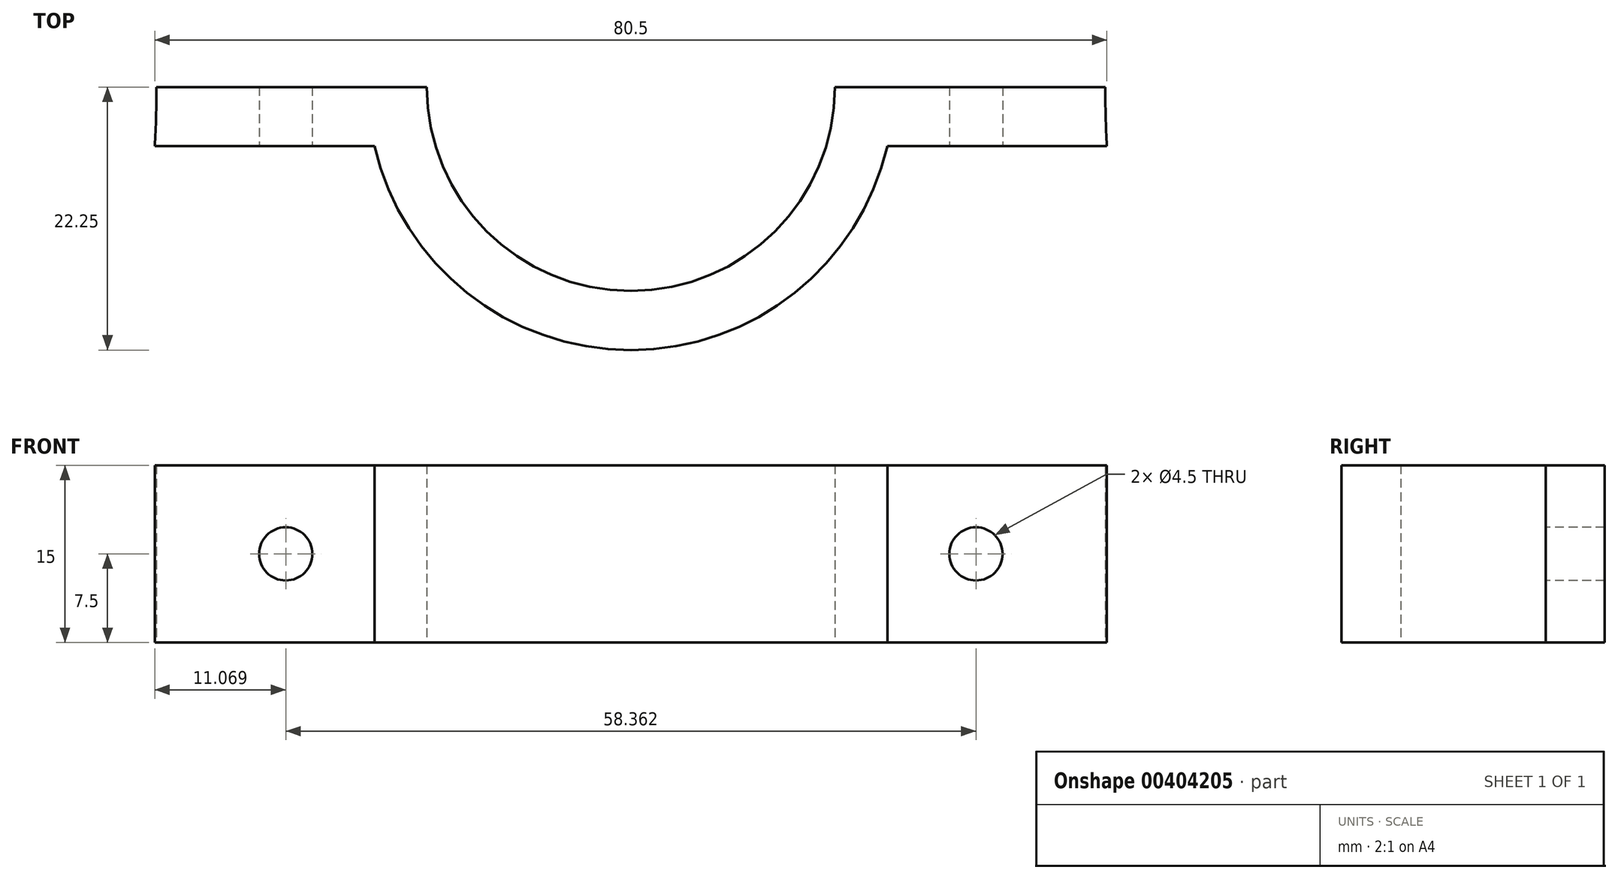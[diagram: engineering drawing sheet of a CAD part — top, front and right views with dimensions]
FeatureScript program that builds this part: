
annotation { "Feature Type Name" : "Feature", "Feature Type Description" : "" }
export const myFeature = defineFeature(function(context is Context, id is Id, definition is map)
    precondition{}
    {
        {
            var Q0;
            Q0=qCreatedBy(makeId("Top.planeOp"),FACE);
            var sketch = newSketch(context, id + "F0", { "sketchPlane" : qUnion([Q0])});
            skArc(sketch, "E0", {"start": v(17.25, 0) * mm, "mid": v(0, -17.25) * mm, "end": v(-17.25, 0) * mm});
            skArc(sketch, "E1", {"start": v(21.68, -5) * mm, "mid": v(0, -22.25) * mm, "end": v(-21.68, -5) * mm});
            skLineSegment(sketch, "E2", {"start": v(-21.68, -5) * mm, "end": v(-40.25, -5) * mm});
            skLineSegment(sketch, "E3", {"start": v(-40.1, 0) * mm, "end": v(-17.25, 0) * mm});
            skLineSegment(sketch, "E4.MirrorCS", {"start": v(40.1, 0) * mm, "end": v(17.25, 0) * mm});
            skLineSegment(sketch, "E5.MirrorCS", {"start": v(40.25, -5) * mm, "end": v(40.25, 0) * mm, "construction": true});
            skLineSegment(sketch, "E6.MirrorCS", {"start": v(21.68, -5) * mm, "end": v(40.25, -5) * mm});
            skArc(sketch, "E7", {"start": v(-40.1, 0) * mm, "mid": v(-40.14, -2.5) * mm, "end": v(-40.25, -5) * mm});
            skPoint(sketch, "E8.end.orphan", {"position": v(-40.25, 0) * mm});
            skArc(sketch, "E9.MirrorCS", {"start": v(40.1, 0) * mm, "mid": v(40.14, -2.5) * mm, "end": v(40.25, -5) * mm});
            skPoint(sketch, "E10.orphan", {"position": v(40.25, 0) * mm});
            skSolve(sketch);
        }
        {
            var Q0;
            Q0 = qSketchRegion(id + "F0", true);
            extrude(context, id + "F1", {"entities" : qUnion([Q0]), "endBound" : BoundingType.SYMMETRIC, "depth" : 15 * mm});
        }
        {
            var Q0;
            Q0=makeQuery(id+"F1.opExtrude","SWEPT_FACE",FACE,{"disambiguationData":[OSD([sQuery(id+"F0.wireOp",EDGE,"E2")])]});
            var sketch = newSketch(context, id + "F2", { "sketchPlane" : qUnion([Q0])});
            skCircle(sketch, "E11", {"center": v(-29.18, 0) * mm, "radius": 2.25 * mm});
            skCircle(sketch, "E12.MirrorC", {"center": v(29.18, 0) * mm, "radius": 2.25 * mm});
            skSolve(sketch);
        }
        {
            var Q0;
            Q0 = qSketchRegion(id + "F2", true);
            extrude(context, id + "F3", {"entities" : qUnion([Q0]), "operationType" : NewBodyOperationType.REMOVE, "oppositeDirection" : true, "depth" : 25 * mm});
        }
    });
